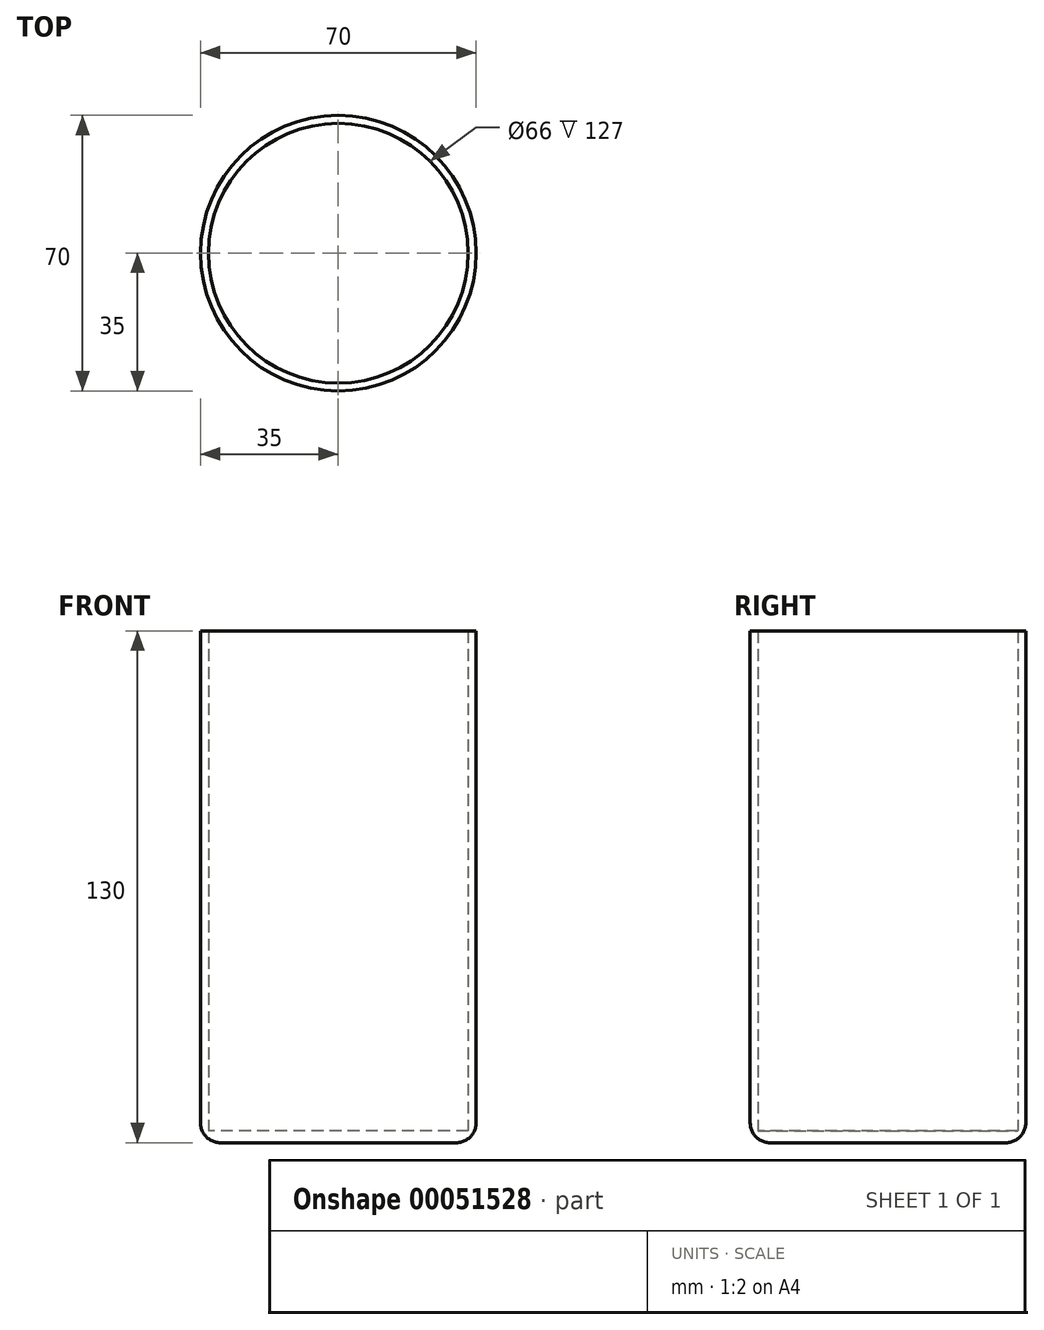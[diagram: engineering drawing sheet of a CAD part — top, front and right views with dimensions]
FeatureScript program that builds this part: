
annotation { "Feature Type Name" : "Feature", "Feature Type Description" : "" }
export const myFeature = defineFeature(function(context is Context, id is Id, definition is map)
    precondition{}
    {
        {
            var Q0;
            Q0=qCreatedBy(makeId("Top.planeOp"),FACE);
            var sketch = newSketch(context, id + "F0", { "sketchPlane" : qUnion([Q0])});
            skCircle(sketch, "E0", {"center": v(0, 0) * mm, "radius": 35 * mm});
            skCircle(sketch, "E1", {"center": v(0, 0) * mm, "radius": 33 * mm});
            skSolve(sketch);
        }
        {
            var Q0;
            Q0=makeQuery(id+"F0.imprint","IMPRINT",FACE,{"disambiguationData":[TD([[makeQuery(id+"F0.imprint","IMPRINT",EDGE,{"derivedFrom":sQuery(id+"F0.wireOp",EDGE,"E0")}),1.0]])]});
            extrude(context, id + "F1", {"entities" : qUnion([Q0]), "depth" : 130 * mm});
        }
        {
            var Q0;
            Q0=qCreatedBy(makeId("Top.planeOp"),FACE);
            var sketch = newSketch(context, id + "F2", { "sketchPlane" : qUnion([Q0])});
            skCircle(sketch, "E2", {"center": v(0, 0) * mm, "radius": 35 * mm});
            skSolve(sketch);
        }
        {
            var Q0;
            Q0 = qSketchRegion(id + "F2", true);
            extrude(context, id + "F3", {"entities" : qUnion([Q0]), "operationType" : NewBodyOperationType.ADD, "depth" : 3 * mm});
        }
        {
            var Q0;
            Q0=makeQuery(id+"F1.opExtrude","CAP_EDGE",EDGE,{"disambiguationData":[OSD([sQuery(id+"F0.wireOp",EDGE,"E0")])],"isStart":true});
            fillet(context, id + "F4", {"entities" : qUnion([Q0]), "radius" : 5 * mm, "tangentPropagation" : true, "allowEdgeOverflow" : false});
        }
    });
